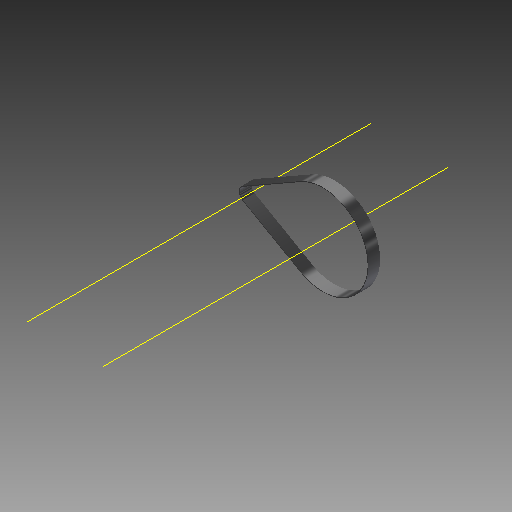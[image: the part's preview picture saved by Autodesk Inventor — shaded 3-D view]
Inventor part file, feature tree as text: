
AUTODESK INVENTOR PART (.ipt)
format: ipt  version: 2017 (Build 210142000, 142)  size: 97,280 bytes
history: native  units: mm (DEFAULTED — no unit token found)
features: other x4, plane x2, sketch x1, sweep x1
ambient origin geometry x8: Origin, YZ Plane, XZ Plane, XY Plane, X Axis, Y Axis, Z Axis, Center Point
bodies: Solid1 (feature_tree)
feature tree (8):
  sketch  "Sketch Path"  dims[d0=10.0mm d2=0.0mm d4=0.3mm d5=0.3mm d6=0.0mm d7=0.0mm d8=0.0mm d9=0.0mm d10=0.0mm d11=0.0mm]
  other  "Cross Section Plane"
  other  "Work Axis1"
  other  "Work Axis2"
  plane  "Work Plane2"
  plane  "Work Plane3"
  sweep  "Belt"
  other  "Cross Section"
